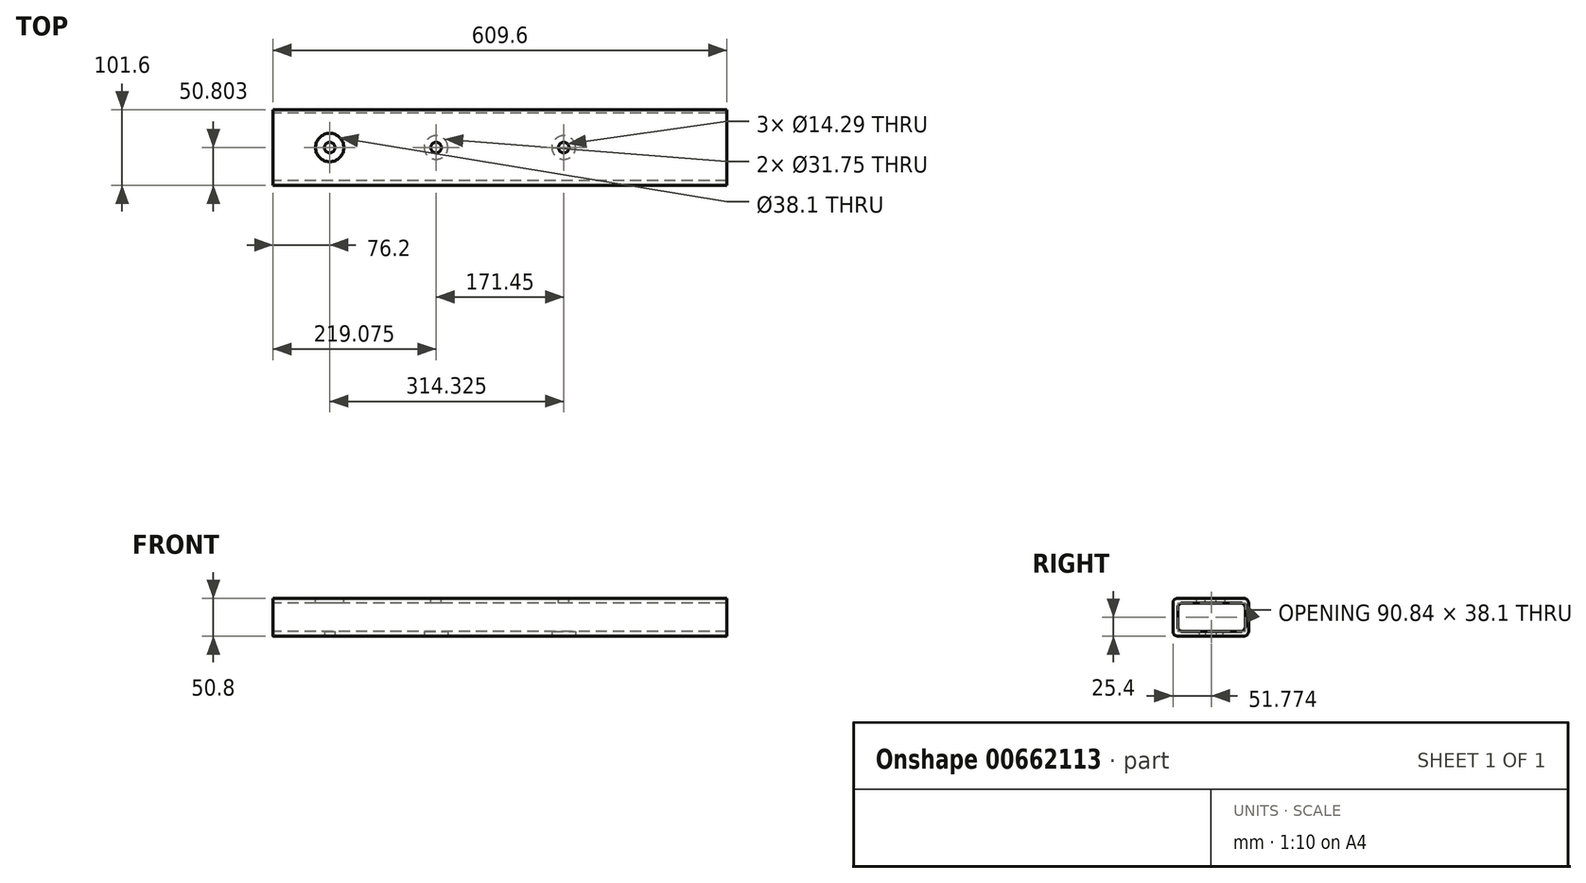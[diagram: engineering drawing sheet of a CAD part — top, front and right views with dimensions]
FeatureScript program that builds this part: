
annotation { "Feature Type Name" : "Feature", "Feature Type Description" : "" }
export const myFeature = defineFeature(function(context is Context, id is Id, definition is map)
    precondition{}
    {
        {
            var Q0;
            Q0=qCreatedBy(makeId("Top.planeOp"),FACE);
            var sketch = newSketch(context, id + "F0", { "sketchPlane" : qUnion([Q0])});
            skLineSegment(sketch, "E0.bottom", {"start": v(-35.83, 88.13) * mm, "end": v(573.77, 88.13) * mm});
            skLineSegment(sketch, "E0.top", {"start": v(-35.83, -13.47) * mm, "end": v(573.77, -13.47) * mm});
            skLineSegment(sketch, "E0.left", {"start": v(-35.83, 88.13) * mm, "end": v(-35.83, -13.47) * mm});
            skLineSegment(sketch, "E0.right", {"start": v(573.77, 88.13) * mm, "end": v(573.77, -13.47) * mm});
            skSolve(sketch);
        }
        {
            var Q0;
            Q0=qCreatedBy(makeId("Right.planeOp"),FACE);
            var sketch = newSketch(context, id + "F1", { "sketchPlane" : qUnion([Q0])});
            skLineSegment(sketch, "E1", {"start": v(-266.68, 50.8) * mm, "end": v(-177.78, 50.8) * mm});
            skLineSegment(sketch, "E2", {"start": v(-171.43, 44.45) * mm, "end": v(-171.43, 6.35) * mm});
            skLineSegment(sketch, "E3", {"start": v(-177.78, 0) * mm, "end": v(-266.68, 0) * mm});
            skLineSegment(sketch, "E4", {"start": v(-273.03, 6.35) * mm, "end": v(-273.03, 44.45) * mm});
            skLineSegment(sketch, "E5", {"start": v(-273.03, 37.77) * mm, "end": v(-266.68, 37.77) * mm});
            skLineSegment(sketch, "E6", {"start": v(-260.32, 44.45) * mm, "end": v(-182.19, 44.45) * mm});
            skLineSegment(sketch, "E7", {"start": v(-175.84, 38.1) * mm, "end": v(-175.84, 12.7) * mm});
            skLineSegment(sketch, "E8", {"start": v(-182.19, 6.35) * mm, "end": v(-260.33, 6.35) * mm});
            skLineSegment(sketch, "E9", {"start": v(-266.67, 38.1) * mm, "end": v(-266.68, 12.7) * mm});
            skPoint(sketch, "E10.visualSharp", {"position": v(-266.67, 44.45) * mm});
            skArc(sketch, "E10.filletArc", {"start": v(-260.32, 44.45) * mm, "mid": v(-264.81, 42.6) * mm, "end": v(-266.67, 38.1) * mm});
            skPoint(sketch, "E11.visualSharp", {"position": v(-175.84, 44.45) * mm});
            skArc(sketch, "E11.filletArc", {"start": v(-175.84, 38.1) * mm, "mid": v(-177.7, 42.6) * mm, "end": v(-182.19, 44.45) * mm});
            skPoint(sketch, "E12.visualSharp", {"position": v(-175.84, 6.35) * mm});
            skArc(sketch, "E12.filletArc", {"start": v(-182.19, 6.35) * mm, "mid": v(-177.7, 8.2) * mm, "end": v(-175.84, 12.7) * mm});
            skPoint(sketch, "E13.visualSharp", {"position": v(-266.68, 6.35) * mm});
            skArc(sketch, "E13.filletArc", {"start": v(-266.68, 12.7) * mm, "mid": v(-264.82, 8.21) * mm, "end": v(-260.33, 6.35) * mm});
            skPoint(sketch, "E14.visualSharp", {"position": v(-273.03, 0) * mm});
            skArc(sketch, "E14.filletArc", {"start": v(-273.03, 6.35) * mm, "mid": v(-271.17, 1.86) * mm, "end": v(-266.68, 0) * mm});
            skPoint(sketch, "E15.visualSharp", {"position": v(-273.03, 50.8) * mm});
            skArc(sketch, "E15.filletArc", {"start": v(-266.68, 50.8) * mm, "mid": v(-271.17, 48.94) * mm, "end": v(-273.03, 44.45) * mm});
            skPoint(sketch, "E16.visualSharp", {"position": v(-171.43, 50.8) * mm});
            skArc(sketch, "E16.filletArc", {"start": v(-171.43, 44.45) * mm, "mid": v(-173.29, 48.94) * mm, "end": v(-177.78, 50.8) * mm});
            skPoint(sketch, "E17.visualSharp", {"position": v(-171.43, 0) * mm});
            skArc(sketch, "E17.filletArc", {"start": v(-177.78, 0) * mm, "mid": v(-173.29, 1.86) * mm, "end": v(-171.43, 6.35) * mm});
            skSolve(sketch);
        }
        {
            var Q0;
            Q0 = qSketchRegion(id + "F1", true);
            extrude(context, id + "F2", {"entities" : qUnion([Q0]), "endBound" : BoundingType.SYMMETRIC, "depth" : 609.6 * mm, "offsetDistance" : 25.4 * mm});
        }
        {
            var Q0;
            Q0=makeQuery(id+"F2.opExtrude","SWEPT_FACE",FACE,{"disambiguationData":[OSD([sQuery(id+"F1.wireOp",EDGE,"E1")])]});
            var sketch = newSketch(context, id + "F3", { "sketchPlane" : qUnion([Q0])});
            skPoint(sketch, "E18", {"position": v(-228.6, -222.23) * mm});
            skPoint(sketch, "E19", {"position": v(-85.72, -222.23) * mm});
            skPoint(sketch, "E20", {"position": v(85.72, -222.23) * mm});
            skSolve(sketch);
        }
        {
            var Q0;
            Q0=sQuery(id+"F3.wireOp",VERTEX,"E19");
            var Q1;
            Q1=sQuery(id+"F3.wireOp",VERTEX,"E20");
            var Q2;
            Q2=makeQuery(id+"F2.opExtrude","SWEPT_BODY",BODY,{"disambiguationData":[OSD([sQuery(id+"F1.wireOp",EDGE,"E1"),sQuery(id+"F1.wireOp",EDGE,"E2"),sQuery(id+"F1.wireOp",EDGE,"E3"),sQuery(id+"F1.wireOp",EDGE,"E4"),sQuery(id+"F1.wireOp",EDGE,"E6"),sQuery(id+"F1.wireOp",EDGE,"E7"),sQuery(id+"F1.wireOp",EDGE,"E8"),sQuery(id+"F1.wireOp",EDGE,"E9"),sQuery(id+"F1.wireOp",EDGE,"E10.filletArc"),sQuery(id+"F1.wireOp",EDGE,"E11.filletArc"),sQuery(id+"F1.wireOp",EDGE,"E12.filletArc"),sQuery(id+"F1.wireOp",EDGE,"E13.filletArc"),sQuery(id+"F1.wireOp",EDGE,"E14.filletArc"),sQuery(id+"F1.wireOp",EDGE,"E15.filletArc"),sQuery(id+"F1.wireOp",EDGE,"E16.filletArc"),sQuery(id+"F1.wireOp",EDGE,"E17.filletArc")])]});
            hole(context, id + "F4", {"style" : HoleStyle.SIMPLE, "endStyle" : HoleEndStyle.BLIND, "holeDiameter" : 14.29 * mm, "majorDiameter" : 6.35 * mm, "holeDepth" : 6.35 * mm, "isTappedThrough" : true, "tappedDepth" : 12.7 * mm, "tapClearance" : 3, "startFromSketch" : true, "locations" : qUnion([Q0, Q1]), "scope" : qUnion([Q2])});
        }
        {
            var Q0;
            Q0=makeQuery(id+"F2.opExtrude","SWEPT_FACE",FACE,{"disambiguationData":[OSD([sQuery(id+"F1.wireOp",EDGE,"E1")])]});
            var sketch = newSketch(context, id + "F5", { "sketchPlane" : qUnion([Q0])});
            skPoint(sketch, "E21", {"position": v(-228.6, -222.23) * mm});
            skSolve(sketch);
        }
        {
            var Q0;
            Q0=sQuery(id+"F5.wireOp",VERTEX,"E21");
            var Q1;
            Q1=makeQuery(id+"F2.opExtrude","SWEPT_BODY",BODY,{"disambiguationData":[OSD([sQuery(id+"F1.wireOp",EDGE,"E1"),sQuery(id+"F1.wireOp",EDGE,"E2"),sQuery(id+"F1.wireOp",EDGE,"E3"),sQuery(id+"F1.wireOp",EDGE,"E4"),sQuery(id+"F1.wireOp",EDGE,"E6"),sQuery(id+"F1.wireOp",EDGE,"E7"),sQuery(id+"F1.wireOp",EDGE,"E8"),sQuery(id+"F1.wireOp",EDGE,"E9"),sQuery(id+"F1.wireOp",EDGE,"E10.filletArc"),sQuery(id+"F1.wireOp",EDGE,"E11.filletArc"),sQuery(id+"F1.wireOp",EDGE,"E12.filletArc"),sQuery(id+"F1.wireOp",EDGE,"E13.filletArc"),sQuery(id+"F1.wireOp",EDGE,"E14.filletArc"),sQuery(id+"F1.wireOp",EDGE,"E15.filletArc"),sQuery(id+"F1.wireOp",EDGE,"E16.filletArc"),sQuery(id+"F1.wireOp",EDGE,"E17.filletArc")])]});
            hole(context, id + "F6", {"style" : HoleStyle.SIMPLE, "endStyle" : HoleEndStyle.BLIND, "holeDiameter" : 38.1 * mm, "majorDiameter" : 6.35 * mm, "holeDepth" : 6.35 * mm, "isTappedThrough" : true, "tappedDepth" : 12.7 * mm, "tapClearance" : 3, "startFromSketch" : true, "locations" : qUnion([Q0]), "scope" : qUnion([Q1])});
        }
        {
            var Q0;
            Q0=makeQuery(id+"F2.opExtrude","SWEPT_FACE",FACE,{"disambiguationData":[OSD([sQuery(id+"F1.wireOp",EDGE,"E3")])]});
            var sketch = newSketch(context, id + "F7", { "sketchPlane" : qUnion([Q0])});
            skPoint(sketch, "E22", {"position": v(-228.6, 222.23) * mm});
            skSolve(sketch);
        }
        {
            var Q0;
            Q0=sQuery(id+"F7.wireOp",VERTEX,"E22");
            var Q1;
            Q1=makeQuery(id+"F2.opExtrude","SWEPT_BODY",BODY,{"disambiguationData":[OSD([sQuery(id+"F1.wireOp",EDGE,"E1"),sQuery(id+"F1.wireOp",EDGE,"E2"),sQuery(id+"F1.wireOp",EDGE,"E3"),sQuery(id+"F1.wireOp",EDGE,"E4"),sQuery(id+"F1.wireOp",EDGE,"E6"),sQuery(id+"F1.wireOp",EDGE,"E7"),sQuery(id+"F1.wireOp",EDGE,"E8"),sQuery(id+"F1.wireOp",EDGE,"E9"),sQuery(id+"F1.wireOp",EDGE,"E10.filletArc"),sQuery(id+"F1.wireOp",EDGE,"E11.filletArc"),sQuery(id+"F1.wireOp",EDGE,"E12.filletArc"),sQuery(id+"F1.wireOp",EDGE,"E13.filletArc"),sQuery(id+"F1.wireOp",EDGE,"E14.filletArc"),sQuery(id+"F1.wireOp",EDGE,"E15.filletArc"),sQuery(id+"F1.wireOp",EDGE,"E16.filletArc"),sQuery(id+"F1.wireOp",EDGE,"E17.filletArc")])]});
            hole(context, id + "F8", {"style" : HoleStyle.SIMPLE, "endStyle" : HoleEndStyle.BLIND, "holeDiameter" : 14.29 * mm, "majorDiameter" : 6.35 * mm, "holeDepth" : 6.35 * mm, "isTappedThrough" : true, "tappedDepth" : 12.7 * mm, "tapClearance" : 3, "startFromSketch" : true, "locations" : qUnion([Q0]), "scope" : qUnion([Q1])});
        }
        {
            var Q0;
            Q0=makeQuery(id+"F2.opExtrude","SWEPT_FACE",FACE,{"disambiguationData":[OSD([sQuery(id+"F1.wireOp",EDGE,"E3")])]});
            var sketch = newSketch(context, id + "F9", { "sketchPlane" : qUnion([Q0])});
            skPoint(sketch, "E23", {"position": v(-85.72, 222.23) * mm});
            skPoint(sketch, "E24", {"position": v(85.72, 222.23) * mm});
            skSolve(sketch);
        }
        {
            var Q0;
            Q0=sQuery(id+"F9.wireOp",VERTEX,"E23");
            var Q1;
            Q1=sQuery(id+"F9.wireOp",VERTEX,"E24");
            var Q2;
            Q2=makeQuery(id+"F2.opExtrude","SWEPT_BODY",BODY,{"disambiguationData":[OSD([sQuery(id+"F1.wireOp",EDGE,"E1"),sQuery(id+"F1.wireOp",EDGE,"E2"),sQuery(id+"F1.wireOp",EDGE,"E3"),sQuery(id+"F1.wireOp",EDGE,"E4"),sQuery(id+"F1.wireOp",EDGE,"E6"),sQuery(id+"F1.wireOp",EDGE,"E7"),sQuery(id+"F1.wireOp",EDGE,"E8"),sQuery(id+"F1.wireOp",EDGE,"E9"),sQuery(id+"F1.wireOp",EDGE,"E10.filletArc"),sQuery(id+"F1.wireOp",EDGE,"E11.filletArc"),sQuery(id+"F1.wireOp",EDGE,"E12.filletArc"),sQuery(id+"F1.wireOp",EDGE,"E13.filletArc"),sQuery(id+"F1.wireOp",EDGE,"E14.filletArc"),sQuery(id+"F1.wireOp",EDGE,"E15.filletArc"),sQuery(id+"F1.wireOp",EDGE,"E16.filletArc"),sQuery(id+"F1.wireOp",EDGE,"E17.filletArc")])]});
            hole(context, id + "F10", {"style" : HoleStyle.SIMPLE, "endStyle" : HoleEndStyle.BLIND, "holeDiameter" : 31.75 * mm, "majorDiameter" : 6.35 * mm, "holeDepth" : 6.35 * mm, "isTappedThrough" : true, "tappedDepth" : 12.7 * mm, "tapClearance" : 3, "startFromSketch" : true, "locations" : qUnion([Q0, Q1]), "scope" : qUnion([Q2])});
        }
    });
